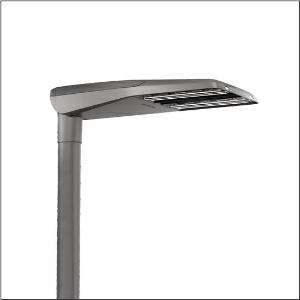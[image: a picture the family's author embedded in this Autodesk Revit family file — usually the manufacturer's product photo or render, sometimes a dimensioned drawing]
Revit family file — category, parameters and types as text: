
# Revit family: streetlight_sl_11_iq_midi___st1_2a_5xc3a21f08me_5047
name_source: partatom
category: Lighting Fixtures
units: mm (PartAtom-declared; Revit-internal decimal feet)

## family parameters
Cut with Voids When Loaded = No
Host = Face
Light Source = No
Part Type = Normal
Room Calculation Point = No
Round Connector Dimension = Use Diameter
Shared = No

## types (1)
- --- (1 x LED, 14840 lm, 124.7 W, 2200K)
    Apparent Load = 125 VA
    CIE Flux Codes = 32 70 96 100 100
    Color Rendering = 70
    Color Temperature = 2200K
    Default Elevation = 1800 mm
    Description = Streetlight SL 11 iQ midi, mast luminaire, primary light control with 3 zone facetted reflector, of plastic, silver coated, highly specular, primary optical cover: cover, of PMMA, transparent, light distribution: ST1.2a, light emission: direct distribution, primary light characteristic: asymmetric, installation type: post-top, side-entry, LED, High Power LED, rated luminous flux: 14.840lm, luminous efficacy: 119lm/W, light colour: 722, colour temperature: 2200K, control: Street-Remote, optimised constant luminous flux control (CLO 2.0), Desk-Remote (wireless, voltage-free reading and setting of iQ features in the workshop via application-optimized NFC function/RFID function), Light-Fading, Smart-Wire, Night-Set, Lumen-Switch, Temp-Guard, Auto-Match, with cable H07RN-F 5x 1.5mm², mains connection: 230..240V, AC, 50/60Hz, connection cable pre-assembled, cable length: 12,5m, start of lifetime: 125W, end of service life: 132W, reduction: 57W, luminaire housing, of diecast aluminium, powder-coated, Siteco® metallic grey (DB 702S), please order mast flange separately, inclination adjustable without tools: 0°, 5°, 10°, 15° (post-top) | 0°, -5°, -10°, -15° (side-entry), sealing non-destructively replaceable, multi-level sealing system, length: 780mm, width: 376mm, height: 118mm, mast flange for spigot size: 42mm (side-entry): 5XC10008XM4, 60/48mm (side-entry/post-top): 5XC10108XM2, 76/60mm (side-entry/post-top): 5XC10108XM1, equipment: Power, protection rating (complete): IP66, insulation class (complete): insulation class II (safety insulation), certification: CE, ENEC, VDE, impact resistance: IK09, permissible operating ambient temperature for outdoor applications: -25..+50°C, standard-compliant lighting for roads and squares, Environmental Product Declaration (EPD) tested and certified by an independent institute, packaging unit: 1 piece

Light Distribution: ST1.2a
    Height = 118 mm
    Lamp = 1 x LED
    Lamp Light Flux = 14840 lm
    Lamp Power = 124.7 W
    Lamp count = 1
    Length = 780 mm
    Luminous efficacy = 119 lm/W
    Manufacturer = Siteco
    ModVariant = No
    Model = 5XC3A21F08ME
    Number of Poles = 1
    OnlyDefault = Yes
    Power Factor = 1
    Product Name = Streetlight SL 11 iQ midi | ST1.2a
    Product group = mast luminaire | pylon top
    ProductGroupID = 6100
    Protection Class = Protection class II
    Protection Degree = IP 66
    RLX_Detail_Level = 1
    RLX_Emergency_Light_Flux = 0 lm
    RLX_Emergency_Type = 0
    RLX_Emergency_Type_DB = No
    RlxData = <blob elided: 70661 chars, md5=ad408d92>
    Socket = socket
    Standby Power = 0 W
    System Light Flux = 14841 lm
    System Power = 125 W
    Type Comments = factory setting: luminous flux: 100 % | dim-lin: 254 | 557 mA
    Type Image = l_1005960.jpg
    URL = http://relux.com
    VarID = @adj_079121
    Voltage = 0 V
    Weight = 0.00 kg
    Width = 376 mm

## geometry (parser evidence)
native form markers: Blend x4, Sweep x10
no freeform markers — native parametric forms only
